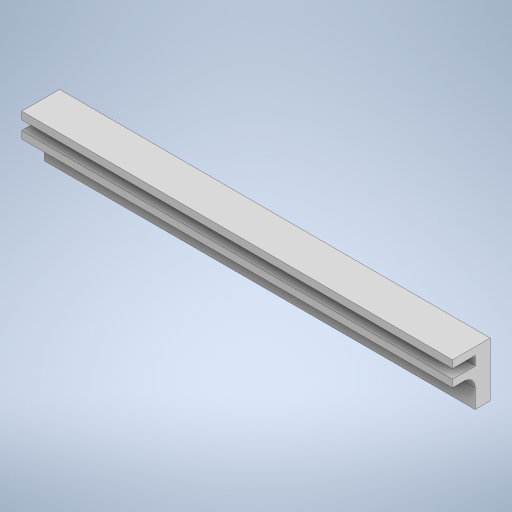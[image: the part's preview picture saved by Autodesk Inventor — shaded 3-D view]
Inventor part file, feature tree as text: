
AUTODESK INVENTOR PART (.ipt)
format: ipt  version: 2023 (Build 270158000, 158)  size: 283,648 bytes
history: native  units: in
note: dims shown in document units (in); Inventor stores cm internally (conversion verified against a paired STEP export)
features: extrude x4, sketch x4, fillet x1
ambient origin geometry x8: Origin, YZ Plane, XZ Plane, XY Plane, X Axis, Y Axis, Z Axis, Center Point
bodies: Solid1 (feature_tree)
feature tree (9):
  extrude  "Extrusion1"  Depth=1.4173in
  extrude  "Extrusion2"  Depth=0.1969in
  extrude  "Extrusion3"  Depth=0.1969in
  fillet  "Fillet1"  Radius=0.5906in
  extrude  "Extrusion4"  Depth=0.1969in
  sketch  "Sketch1"  dims[d0=11.2205in d1=1.4173in]
  sketch  "Sketch4"  dims[d2=0.3937in d3=0.0in d4=0.1969in]
  sketch  "Sketch5"  dims[d5=11.2205in d6=0.1969in d7=0.5906in d8=0.0in]
  sketch  "Sketch11"  dims[d9=11.2205in d10=0.1969in d11=0.5906in d12=0.0in d13=0.2953in d47=0.4331in d52=0.1654in d53=0.1654in d54=0.1654in d55=0.0in d56=0.0in d14=0.0in d15=0.0in d16=0.0in]
